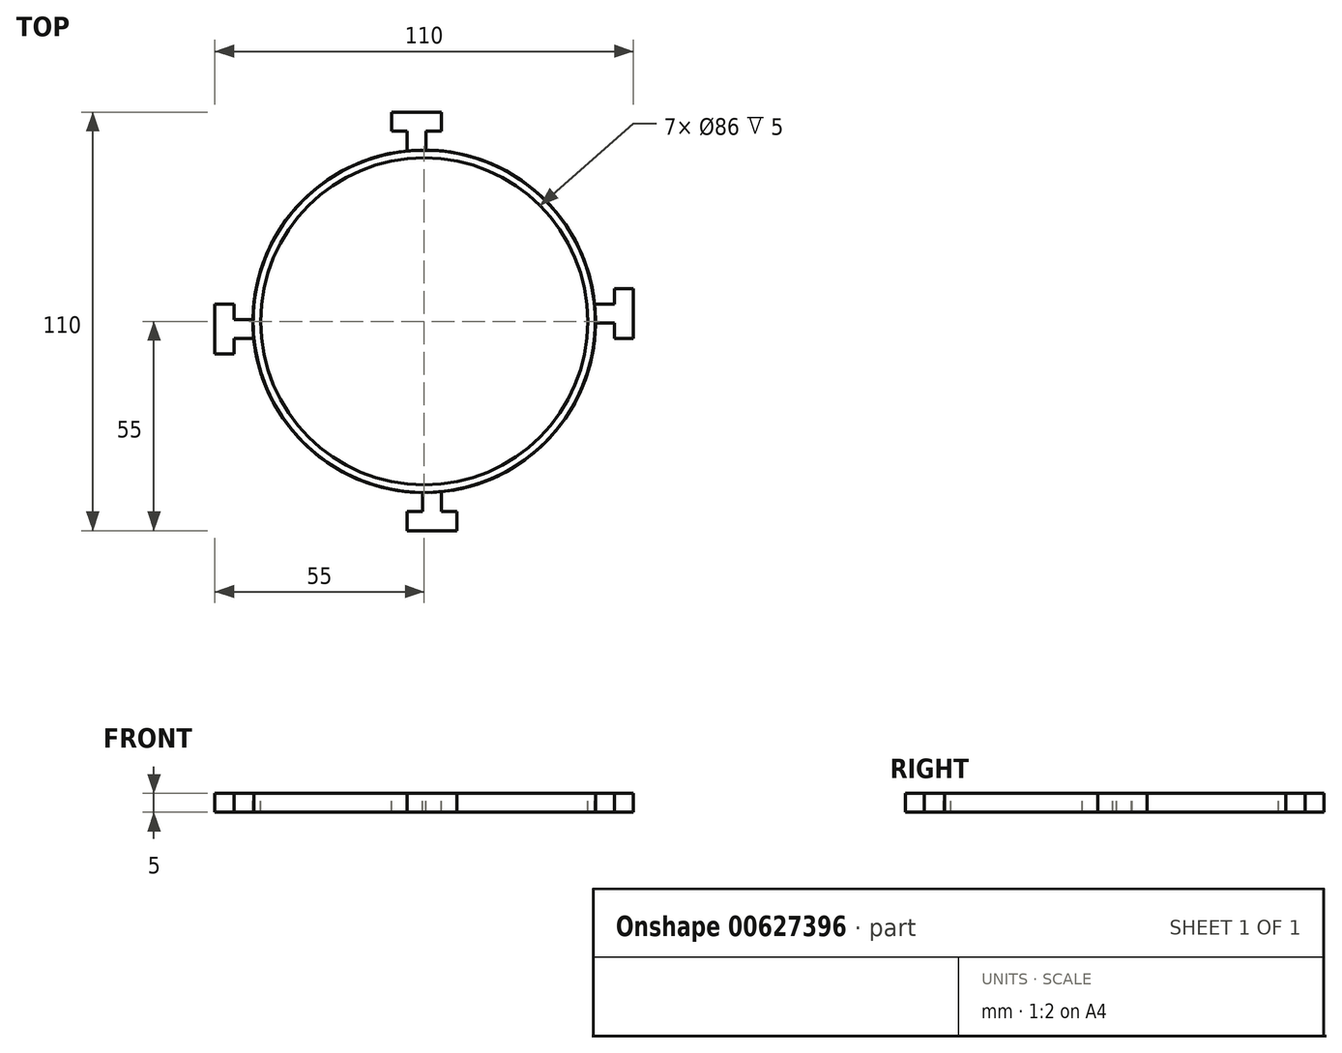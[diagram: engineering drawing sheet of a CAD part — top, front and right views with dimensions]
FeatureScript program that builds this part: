
annotation { "Feature Type Name" : "Feature", "Feature Type Description" : "" }
export const myFeature = defineFeature(function(context is Context, id is Id, definition is map)
    precondition{}
    {
        {
            var Q0;
            Q0=qCreatedBy(makeId("Top.planeOp"),FACE);
            var sketch = newSketch(context, id + "F0", { "sketchPlane" : qUnion([Q0])});
            skCircle(sketch, "E0", {"center": v(0, 0) * mm, "radius": 45 * mm});
            skSolve(sketch);
        }
        {
            var Q0;
            Q0 = qSketchRegion(id + "F0", true);
            extrude(context, id + "F1", {"entities" : qUnion([Q0]), "depth" : 5 * mm, "offsetDistance" : 25.4 * mm});
        }
        {
            var Q0;
            Q0=makeQuery(id+"F1.opExtrude","CAP_FACE",FACE,{"disambiguationData":[OSD([sQuery(id+"F0.wireOp",EDGE,"E0")])],"isStart":false});
            var sketch = newSketch(context, id + "F2", { "sketchPlane" : qUnion([Q0])});
            skCircle(sketch, "E1", {"center": v(0, 0) * mm, "radius": 43 * mm});
            skSolve(sketch);
        }
        {
            var Q0;
            Q0=makeQuery(id+"F2.imprint","IMPRINT",FACE,{"disambiguationData":[TD([[makeQuery(id+"F2.imprint","IMPRINT",EDGE,{"derivedFrom":sQuery(id+"F2.wireOp",EDGE,"E1")}),1.0]])]});
            extrude(context, id + "F3", {"entities" : qUnion([Q0]), "operationType" : NewBodyOperationType.REMOVE, "oppositeDirection" : true, "depth" : 25.4 * mm, "offsetDistance" : 25.4 * mm});
        }
        {
            var Q0;
            Q0=makeQuery(id+"F1.opExtrude","CAP_FACE",FACE,{"disambiguationData":[OSD([sQuery(id+"F0.wireOp",EDGE,"E0")])],"isStart":false});
            var sketch = newSketch(context, id + "F4", { "sketchPlane" : qUnion([Q0])});
            skLineSegment(sketch, "E2", {"start": v(4.53, -44.77) * mm, "end": v(4.53, -50) * mm});
            skLineSegment(sketch, "E3", {"start": v(4.53, -50) * mm, "end": v(8.53, -50) * mm});
            skLineSegment(sketch, "E4", {"start": v(8.53, -50) * mm, "end": v(8.53, -55) * mm});
            skLineSegment(sketch, "E5", {"start": v(8.53, -55) * mm, "end": v(-4.46, -55) * mm});
            skLineSegment(sketch, "E6", {"start": v(-4.46, -55) * mm, "end": v(-4.46, -50) * mm});
            skLineSegment(sketch, "E7", {"start": v(-4.46, -50) * mm, "end": v(-0.46, -50) * mm});
            skLineSegment(sketch, "E8", {"start": v(-0.46, -50) * mm, "end": v(-0.46, -45) * mm});
            skLineSegment(sketch, "E9", {"start": v(4.53, -44.77) * mm, "end": v(-0.46, -45) * mm});
            skSolve(sketch);
        }
        {
            var Q0;
            {var subQ0=sQuery(id+"F4.wireOp",EDGE,"E2");Q0=makeQuery(id+"F4.imprint","IMPRINT",FACE,{"disambiguationData":[TD([[makeQuery(id+"F4.imprint","IMPRINT",EDGE,{"derivedFrom":subQ0}),-1.0]])]});}
            extrude(context, id + "F5", {"entities" : qUnion([Q0]), "operationType" : NewBodyOperationType.ADD, "oppositeDirection" : true, "depth" : 5 * mm, "offsetDistance" : 25.4 * mm});
        }
        {
            var Q0;
            Q0=makeQuery(id+"F1.opExtrude","SWEPT_BODY",BODY,{"disambiguationData":[OSD([sQuery(id+"F0.wireOp",EDGE,"E0")])]});
            var Q1;
            Q1=makeQuery(id+"F3.boolean.opBoolean","INTERSECT",EDGE,{"derivedFrom":[makeQuery(id+"F1.opExtrude","CAP_FACE",FACE,{"disambiguationData":[OSD([sQuery(id+"F0.wireOp",EDGE,"E0")])],"isStart":true}),makeQuery(id+"F3.opExtrude","SWEPT_FACE",FACE,{"disambiguationData":[OSD([sQuery(id+"F2.wireOp",EDGE,"E1")])]})]});
            circularPattern(context, id + "F6", {"entities" : qUnion([Q0]), "axis" : qUnion([Q1]), "angle" : 360 * degree, "instanceCount" : 4, "oppositeDirection" : true, "equalSpace" : true, "isCentered" : true});
        }
    });
